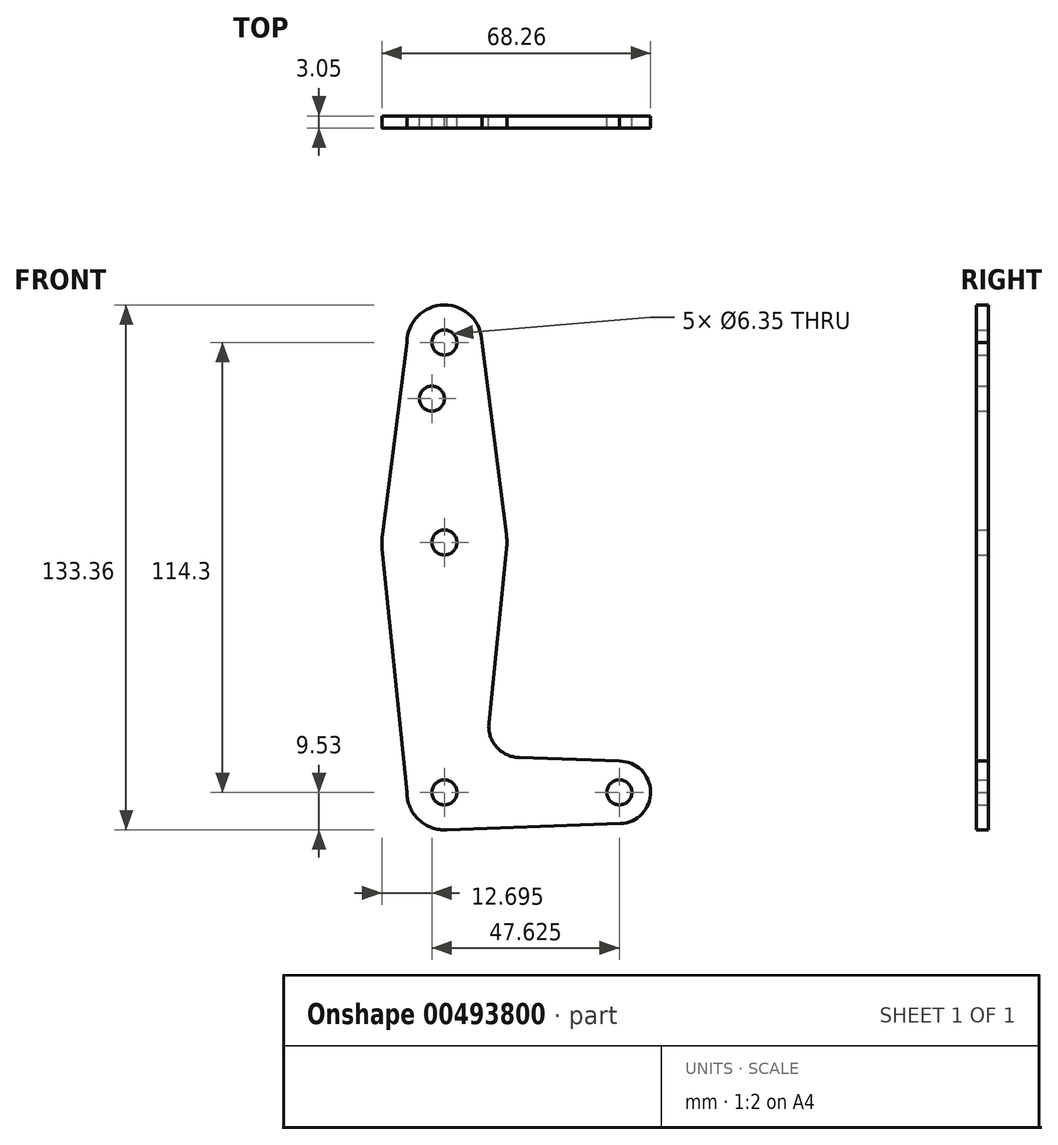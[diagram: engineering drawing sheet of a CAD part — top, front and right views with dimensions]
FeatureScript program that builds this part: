
annotation { "Feature Type Name" : "Feature", "Feature Type Description" : "" }
export const myFeature = defineFeature(function(context is Context, id is Id, definition is map)
    precondition{}
    {
        {
            var Q0;
            Q0=qCreatedBy(makeId("Front.planeOp"),FACE);
            var sketch = newSketch(context, id + "F0", { "sketchPlane" : qUnion([Q0])});
            skLineSegment(sketch, "E0", {"start": v(0, 0) * mm, "end": v(0, 114.3) * mm});
            skLineSegment(sketch, "E1", {"start": v(0, 0) * mm, "end": v(44.45, 0) * mm});
            skCircle(sketch, "E2", {"center": v(0, 0) * mm, "radius": 9.53 * mm});
            skCircle(sketch, "E3", {"center": v(0, 63.5) * mm, "radius": 15.88 * mm});
            skCircle(sketch, "E4", {"center": v(0, 114.3) * mm, "radius": 9.53 * mm});
            skCircle(sketch, "E5", {"center": v(44.45, 0) * mm, "radius": 7.94 * mm});
            skLineSegment(sketch, "E6", {"start": v(9.52, 114.3) * mm, "end": v(15.75, 65.5) * mm});
            skLineSegment(sketch, "E7", {"start": v(-9.53, 0) * mm, "end": v(-15.8, 61.9) * mm});
            skLineSegment(sketch, "E8", {"start": v(11.3, 17.6) * mm, "end": v(15.8, 61.9) * mm});
            skLineSegment(sketch, "E9", {"start": v(-9.52, 114.3) * mm, "end": v(-15.75, 65.5) * mm});
            skLineSegment(sketch, "E10", {"start": v(44.45, 7.94) * mm, "end": v(18.93, 8.85) * mm});
            skLineSegment(sketch, "E11", {"start": v(0, -9.53) * mm, "end": v(44.73, -7.93) * mm});
            skCircle(sketch, "E12", {"center": v(0, 114.3) * mm, "radius": 3.18 * mm});
            skCircle(sketch, "E13", {"center": v(0, 63.5) * mm, "radius": 3.18 * mm});
            skCircle(sketch, "E14", {"center": v(0, 0) * mm, "radius": 3.18 * mm});
            skCircle(sketch, "E15", {"center": v(44.45, 0) * mm, "radius": 3.18 * mm});
            skCircle(sketch, "E16", {"center": v(-3.18, 100.03) * mm, "radius": 3.18 * mm});
            skPoint(sketch, "E17.newPointB", {"position": v(0, 9.53) * mm});
            skArc(sketch, "E17.filletArc", {"start": v(11.3, 17.6) * mm, "mid": v(13.22, 11.57) * mm, "end": v(18.93, 8.85) * mm});
            skSolve(sketch);
        }
        {
            var Q0;
            Q0 = qSketchRegion(id + "F0", true);
            var Q1;
            {var subQ0=sQuery(id+"F0.wireOp",EDGE,"E14");var subQ1=sQuery(id+"F0.wireOp",EDGE,"E0");var subQ2=makeQuery(id+"F0.imprint","INTERSECT",VERTEX,{"derivedFrom":[subQ1,subQ0]});Q1=makeQuery(id+"F0.imprint","IMPRINT",FACE,{"disambiguationData":[TD([[makeQuery(id+"F0.imprint","IMPRINT",EDGE,{"disambiguationData":[TD([[subQ2,-1.0]])],"derivedFrom":subQ1}),-1.0]])]});}
            extrude(context, id + "F1", {"entities" : qUnion([Q0, Q1]), "depth" : 3.05 * mm});
        }
    });
